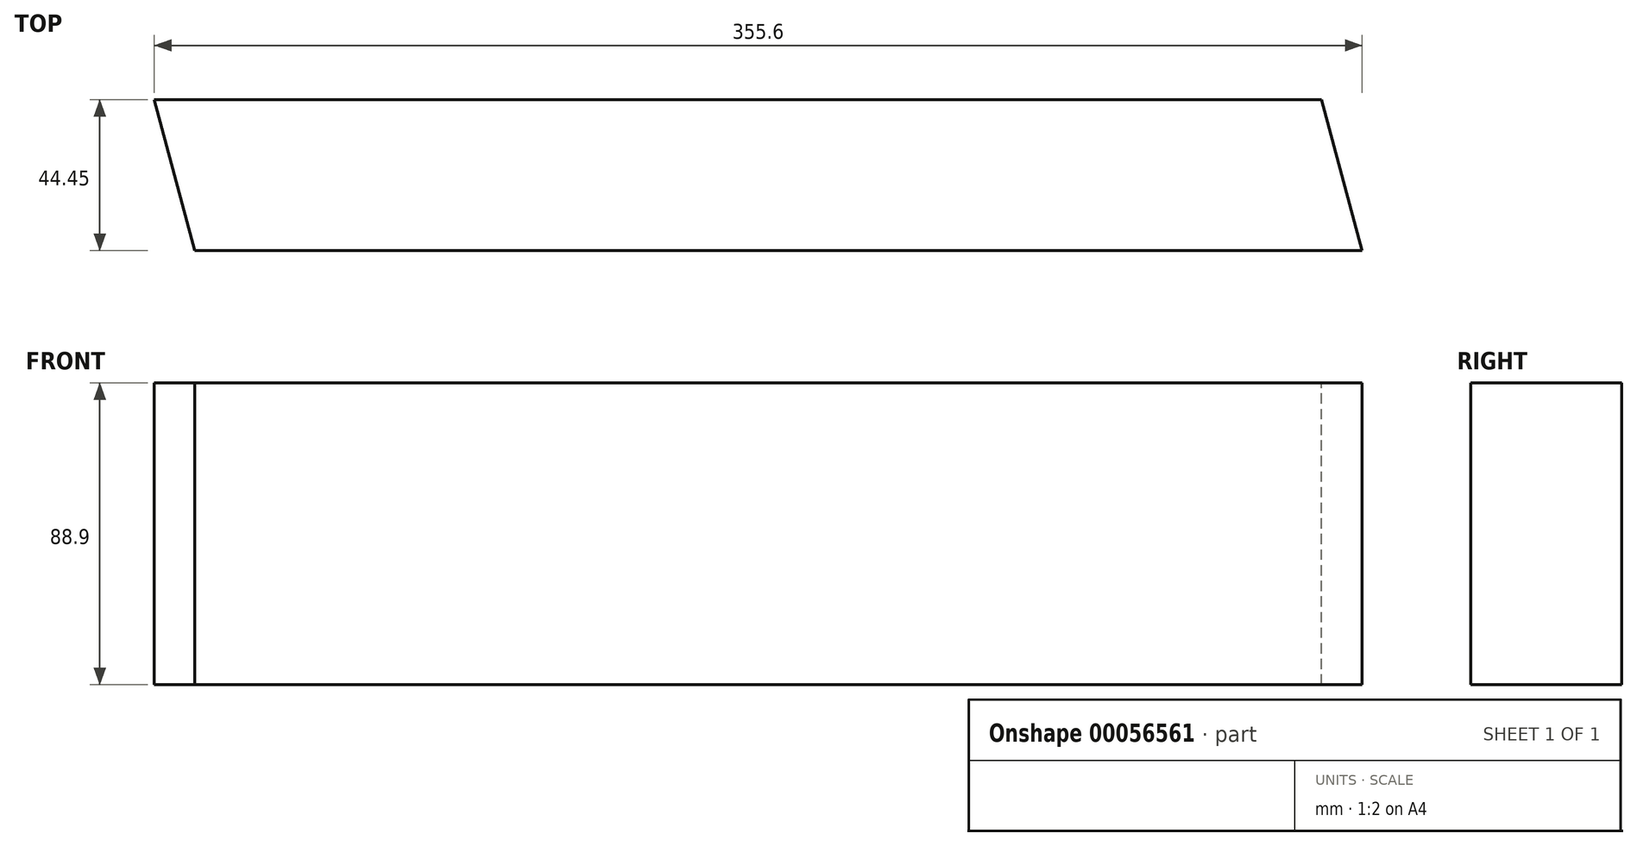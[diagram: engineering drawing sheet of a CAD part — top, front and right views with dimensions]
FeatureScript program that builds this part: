
annotation { "Feature Type Name" : "Feature", "Feature Type Description" : "" }
export const myFeature = defineFeature(function(context is Context, id is Id, definition is map)
    precondition{}
    {
        {
            var Q0;
            Q0=qCreatedBy(makeId("Front.planeOp"),FACE);
            var sketch = newSketch(context, id + "F0", { "sketchPlane" : qUnion([Q0])});
            skLineSegment(sketch, "E0.bottom", {"start": v(0, 0) * mm, "end": v(-355.6, 0) * mm});
            skLineSegment(sketch, "E0.top", {"start": v(0, 88.9) * mm, "end": v(-355.6, 88.9) * mm});
            skLineSegment(sketch, "E0.left", {"start": v(0, 0) * mm, "end": v(0, 88.9) * mm});
            skLineSegment(sketch, "E0.right", {"start": v(-355.6, 0) * mm, "end": v(-355.6, 88.9) * mm});
            skSolve(sketch);
        }
        {
            var Q0;
            Q0=makeQuery(id+"F0.imprint","IMPRINT",FACE,{"disambiguationData":[TD([[makeQuery(id+"F0.imprint","IMPRINT",EDGE,{"derivedFrom":sQuery(id+"F0.wireOp",EDGE,"E0.bottom")}),-1.0]])]});
            extrude(context, id + "F1", {"entities" : qUnion([Q0]), "depth" : 44.45 * mm});
        }
        {
            var Q0;
            Q0=makeQuery(id+"F1.opExtrude","SWEPT_FACE",FACE,{"disambiguationData":[OSD([sQuery(id+"F0.wireOp",EDGE,"E0.top")])]});
            var sketch = newSketch(context, id + "F2", { "sketchPlane" : qUnion([Q0])});
            skLineSegment(sketch, "E1", {"start": v(-355.6, 0) * mm, "end": v(-343.69, -44.45) * mm});
            skLineSegment(sketch, "E2", {"start": v(0, -44.45) * mm, "end": v(-11.91, 0) * mm});
            skSolve(sketch);
        }
        {
            var Q0;
            Q0 = qSketchRegion(id + "F2", true);
            var Q1;
            {var subQ0=sQuery(id+"F2.wireOp",EDGE,"E2");Q1=makeQuery(id+"F2.imprint","IMPRINT",FACE,{"disambiguationData":[TD([[makeQuery(id+"F2.imprint","IMPRINT",EDGE,{"derivedFrom":subQ0}),-1.0]])]});}
            var Q2;
            {var subQ0=sQuery(id+"F2.wireOp",EDGE,"E1");Q2=makeQuery(id+"F2.imprint","IMPRINT",FACE,{"disambiguationData":[TD([[makeQuery(id+"F2.imprint","IMPRINT",EDGE,{"derivedFrom":subQ0}),-1.0]])]});}
            extrude(context, id + "F3", {"entities" : qUnion([Q0, Q1, Q2]), "operationType" : NewBodyOperationType.REMOVE, "oppositeDirection" : true, "depth" : 101.6 * mm});
        }
    });
